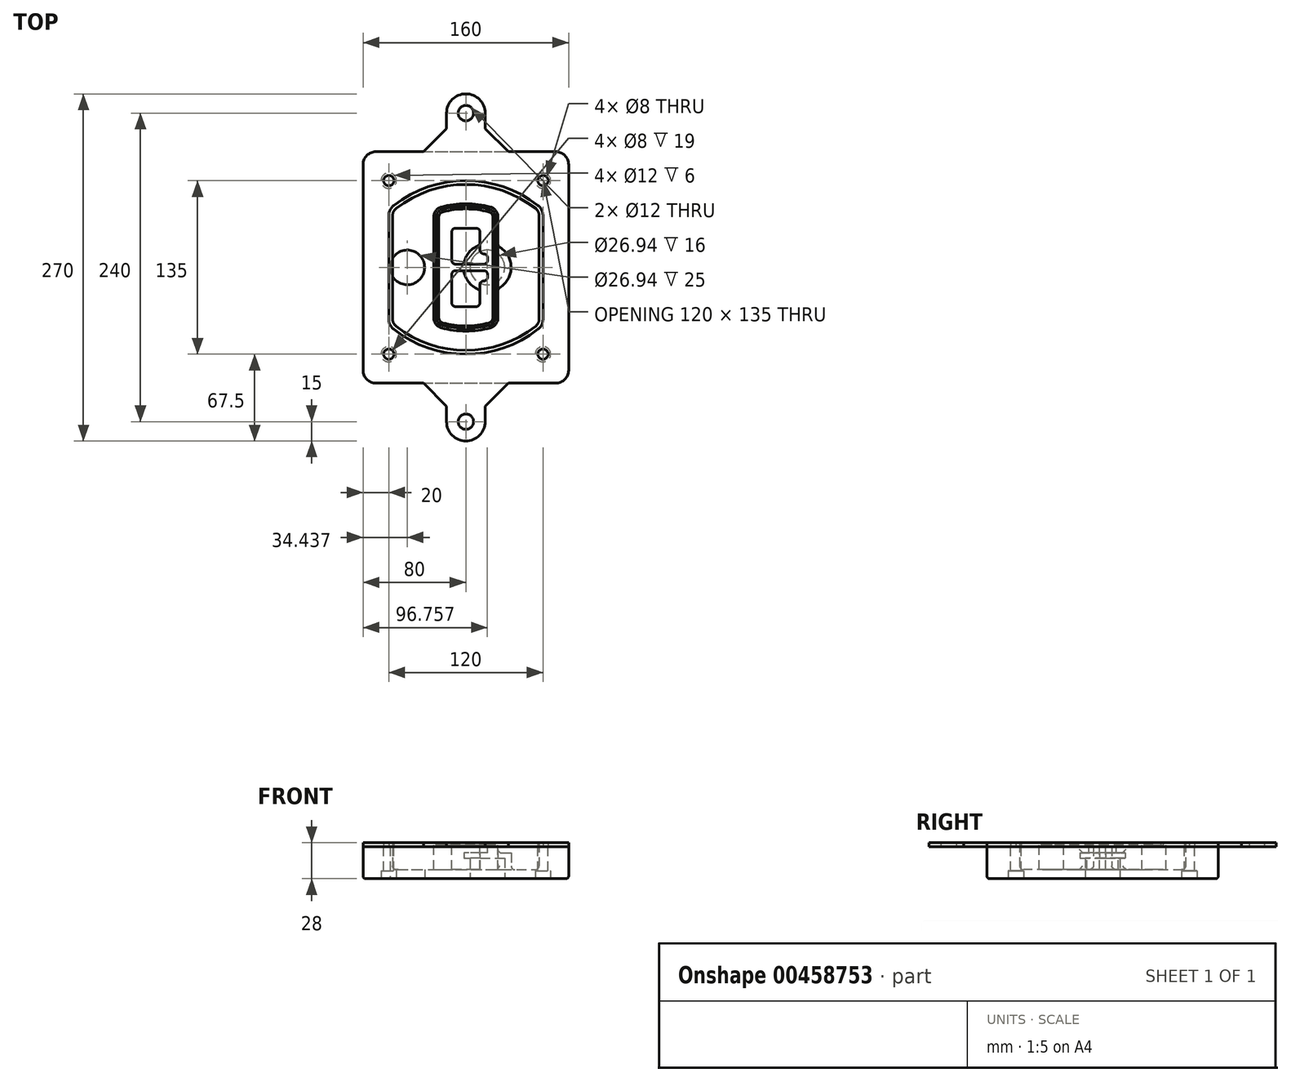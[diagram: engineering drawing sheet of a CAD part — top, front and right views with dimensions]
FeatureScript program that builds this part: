
annotation { "Feature Type Name" : "Feature", "Feature Type Description" : "" }
export const myFeature = defineFeature(function(context is Context, id is Id, definition is map)
    precondition{}
    {
        {
            var Q0;
            Q0=qCreatedBy(makeId("Top.planeOp"),FACE);
            var sketch = newSketch(context, id + "F0", { "sketchPlane" : qUnion([Q0])});
            skPoint(sketch, "E0.rect.middle", {"position": v(0, 0) * mm});
            skLineSegment(sketch, "E1.bottom", {"start": v(-70, -90) * mm, "end": v(70, -90) * mm});
            skLineSegment(sketch, "E1.top", {"start": v(-70, 90) * mm, "end": v(70, 90) * mm});
            skLineSegment(sketch, "E1.left", {"start": v(-80, -80) * mm, "end": v(-80, 80) * mm});
            skLineSegment(sketch, "E1.right", {"start": v(80, -80) * mm, "end": v(80, 80) * mm});
            skLineSegment(sketch, "E2", {"start": v(-80, 90) * mm, "end": v(80, -90) * mm, "construction": true});
            skLineSegment(sketch, "E3", {"start": v(80, 90) * mm, "end": v(-80, -90) * mm, "construction": true});
            skCircle(sketch, "E4", {"center": v(-60, 67.5) * mm, "radius": 4 * mm});
            skCircle(sketch, "E5", {"center": v(60, 67.5) * mm, "radius": 4 * mm});
            skCircle(sketch, "E6", {"center": v(60, -67.5) * mm, "radius": 4 * mm});
            skCircle(sketch, "E7", {"center": v(-60, -67.5) * mm, "radius": 4 * mm});
            skLineSegment(sketch, "E8", {"start": v(-60, 67.5) * mm, "end": v(60, 67.5) * mm, "construction": true});
            skLineSegment(sketch, "E9", {"start": v(60, 67.5) * mm, "end": v(60, -67.5) * mm, "construction": true});
            skLineSegment(sketch, "E10", {"start": v(60, -67.5) * mm, "end": v(-60, -67.5) * mm, "construction": true});
            skLineSegment(sketch, "E11", {"start": v(-60, -67.5) * mm, "end": v(-60, 67.5) * mm, "construction": true});
            skLineSegment(sketch, "E12", {"start": v(-60, 40.3) * mm, "end": v(-60, -40.3) * mm});
            skLineSegment(sketch, "E13", {"start": v(60, 40.3) * mm, "end": v(60, -40.3) * mm});
            skArc(sketch, "E14", {"start": v(56.15, 48.18) * mm, "mid": v(0, 67.5) * mm, "end": v(-56.15, 48.18) * mm});
            skArc(sketch, "E15", {"start": v(-56.15, -48.18) * mm, "mid": v(0, -67.5) * mm, "end": v(56.15, -48.18) * mm});
            skLineSegment(sketch, "E16", {"start": v(-60, 0) * mm, "end": v(60, 0) * mm, "construction": true});
            skPoint(sketch, "E17.visualSharp", {"position": v(-60, -45) * mm});
            skArc(sketch, "E17.filletArc", {"start": v(-60, -40.3) * mm, "mid": v(-58.99, -44.68) * mm, "end": v(-56.15, -48.18) * mm});
            skPoint(sketch, "E18.visualSharp", {"position": v(-60, 45) * mm});
            skArc(sketch, "E18.filletArc", {"start": v(-56.15, 48.18) * mm, "mid": v(-58.99, 44.68) * mm, "end": v(-60, 40.3) * mm});
            skPoint(sketch, "E19.visualSharp", {"position": v(60, 45) * mm});
            skArc(sketch, "E19.filletArc", {"start": v(60, 40.3) * mm, "mid": v(58.99, 44.68) * mm, "end": v(56.15, 48.18) * mm});
            skPoint(sketch, "E20.visualSharp", {"position": v(60, -45) * mm});
            skArc(sketch, "E20.filletArc", {"start": v(56.15, -48.18) * mm, "mid": v(58.99, -44.68) * mm, "end": v(60, -40.3) * mm});
            skPoint(sketch, "E21.visualSharp", {"position": v(-80, 90) * mm});
            skArc(sketch, "E21.filletArc", {"start": v(-70, 90) * mm, "mid": v(-77.07, 87.07) * mm, "end": v(-80, 80) * mm});
            skPoint(sketch, "E22.visualSharp", {"position": v(80, 90) * mm});
            skArc(sketch, "E22.filletArc", {"start": v(80, 80) * mm, "mid": v(77.07, 87.07) * mm, "end": v(70, 90) * mm});
            skPoint(sketch, "E23.visualSharp", {"position": v(80, -90) * mm});
            skArc(sketch, "E23.filletArc", {"start": v(70, -90) * mm, "mid": v(77.07, -87.07) * mm, "end": v(80, -80) * mm});
            skPoint(sketch, "E24.visualSharp", {"position": v(-80, -90) * mm});
            skArc(sketch, "E24.filletArc", {"start": v(-80, -80) * mm, "mid": v(-77.07, -87.07) * mm, "end": v(-70, -90) * mm});
            skArc(sketch, "E25.0", {"start": v(57, 40.3) * mm, "mid": v(56.3, 43.36) * mm, "end": v(54.3, 45.81) * mm});
            skLineSegment(sketch, "E25.1", {"start": v(57, 40.3) * mm, "end": v(57, -40.3) * mm});
            skArc(sketch, "E25.2", {"start": v(54.3, -45.81) * mm, "mid": v(56.3, -43.36) * mm, "end": v(57, -40.3) * mm});
            skArc(sketch, "E25.3", {"start": v(-54.3, -45.81) * mm, "mid": v(0, -64.5) * mm, "end": v(54.3, -45.81) * mm});
            skArc(sketch, "E25.4", {"start": v(-57, -40.3) * mm, "mid": v(-56.3, -43.36) * mm, "end": v(-54.3, -45.81) * mm});
            skArc(sketch, "E25.5", {"start": v(54.3, 45.81) * mm, "mid": v(0, 64.5) * mm, "end": v(-54.3, 45.81) * mm});
            skLineSegment(sketch, "E25.6", {"start": v(-57, 40.3) * mm, "end": v(-57, -40.3) * mm});
            skArc(sketch, "E25.7", {"start": v(-54.3, 45.81) * mm, "mid": v(-56.3, 43.36) * mm, "end": v(-57, 40.3) * mm});
            skArc(sketch, "E26.0", {"start": v(-58.62, 51.33) * mm, "mid": v(-62.58, 46.43) * mm, "end": v(-64, 40.3) * mm});
            skArc(sketch, "E26.1", {"start": v(58.62, 51.33) * mm, "mid": v(0, 71.5) * mm, "end": v(-58.62, 51.33) * mm});
            skArc(sketch, "E26.2", {"start": v(64, 40.3) * mm, "mid": v(62.58, 46.43) * mm, "end": v(58.62, 51.33) * mm});
            skLineSegment(sketch, "E26.3", {"start": v(64, 40.3) * mm, "end": v(64, -40.3) * mm});
            skArc(sketch, "E26.4", {"start": v(58.62, -51.33) * mm, "mid": v(62.58, -46.43) * mm, "end": v(64, -40.3) * mm});
            skLineSegment(sketch, "E26.5", {"start": v(-64, 40.3) * mm, "end": v(-64, -40.3) * mm});
            skArc(sketch, "E26.6", {"start": v(-58.62, -51.33) * mm, "mid": v(0, -71.5) * mm, "end": v(58.62, -51.33) * mm});
            skArc(sketch, "E26.7", {"start": v(-64, -40.3) * mm, "mid": v(-62.58, -46.43) * mm, "end": v(-58.62, -51.33) * mm});
            skSolve(sketch);
        }
        {
            var Q0;
            Q0=makeQuery(id+"F0.imprint","IMPRINT",FACE,{"disambiguationData":[TD([[makeQuery(id+"F0.imprint","IMPRINT",EDGE,{"derivedFrom":sQuery(id+"F0.wireOp",EDGE,"E1.bottom")}),1.0]])]});
            var Q1;
            Q1=makeQuery(id+"F0.imprint","IMPRINT",FACE,{"disambiguationData":[TD([[makeQuery(id+"F0.imprint","IMPRINT",EDGE,{"derivedFrom":sQuery(id+"F0.wireOp",EDGE,"E12")}),1.0]])]});
            var Q2;
            Q2=makeQuery(id+"F0.imprint","IMPRINT",FACE,{"disambiguationData":[TD([[makeQuery(id+"F0.imprint","IMPRINT",EDGE,{"derivedFrom":sQuery(id+"F0.wireOp",EDGE,"E25.0")}),1.0]])]});
            var Q3;
            Q3=makeQuery(id+"F0.imprint","IMPRINT",FACE,{"disambiguationData":[TD([[makeQuery(id+"F0.imprint","IMPRINT",EDGE,{"derivedFrom":sQuery(id+"F0.wireOp",EDGE,"E12")}),-1.0]])]});
            extrude(context, id + "F1", {"entities" : qUnion([Q0, Q1, Q2, Q3]), "oppositeDirection" : true, "depth" : 25 * mm});
        }
        {
            var Q0;
            Q0=makeQuery(id+"F0.imprint","IMPRINT",FACE,{"disambiguationData":[TD([[makeQuery(id+"F0.imprint","IMPRINT",EDGE,{"derivedFrom":sQuery(id+"F0.wireOp",EDGE,"E12")}),1.0]])]});
            extrude(context, id + "F2", {"entities" : qUnion([Q0]), "operationType" : NewBodyOperationType.ADD, "depth" : 3 * mm});
        }
        {
            var Q0;
            Q0=makeQuery(id+"F0.imprint","IMPRINT",FACE,{"disambiguationData":[TD([[makeQuery(id+"F0.imprint","IMPRINT",EDGE,{"derivedFrom":sQuery(id+"F0.wireOp",EDGE,"E25.0")}),1.0]])]});
            extrude(context, id + "F3", {"entities" : qUnion([Q0]), "operationType" : NewBodyOperationType.REMOVE, "oppositeDirection" : true, "depth" : 18 * mm});
        }
        {
            var Q0;
            Q0=makeQuery(id+"F2.opExtrude","CAP_FACE",FACE,{"disambiguationData":[OSD([sQuery(id+"F0.wireOp",EDGE,"E12"),sQuery(id+"F0.wireOp",EDGE,"E13"),sQuery(id+"F0.wireOp",EDGE,"E14"),sQuery(id+"F0.wireOp",EDGE,"E15"),sQuery(id+"F0.wireOp",EDGE,"E17.filletArc"),sQuery(id+"F0.wireOp",EDGE,"E18.filletArc"),sQuery(id+"F0.wireOp",EDGE,"E19.filletArc"),sQuery(id+"F0.wireOp",EDGE,"E20.filletArc"),sQuery(id+"F0.wireOp",EDGE,"E25.0"),sQuery(id+"F0.wireOp",EDGE,"E25.1"),sQuery(id+"F0.wireOp",EDGE,"E25.2"),sQuery(id+"F0.wireOp",EDGE,"E25.3"),sQuery(id+"F0.wireOp",EDGE,"E25.4"),sQuery(id+"F0.wireOp",EDGE,"E25.5"),sQuery(id+"F0.wireOp",EDGE,"E25.6"),sQuery(id+"F0.wireOp",EDGE,"E25.7")])],"isStart":false});
            var sketch = newSketch(context, id + "F4", { "sketchPlane" : qUnion([Q0])});
            skArc(sketch, "E27.0", {"start": v(-19.08, -46.97) * mm, "mid": v(0, -49.5) * mm, "end": v(19.08, -46.97) * mm});
            skArc(sketch, "E28.0", {"start": v(19.08, 46.97) * mm, "mid": v(0, 49.5) * mm, "end": v(-19.08, 46.97) * mm});
            skLineSegment(sketch, "E29", {"start": v(-25, 39.25) * mm, "end": v(-25, -39.25) * mm});
            skLineSegment(sketch, "E30", {"start": v(25, 39.25) * mm, "end": v(25, -39.25) * mm});
            skLineSegment(sketch, "E31", {"start": v(-25, 45.1) * mm, "end": v(25, 45.1) * mm, "construction": true});
            skLineSegment(sketch, "E32", {"start": v(-25, -45.1) * mm, "end": v(25, -45.1) * mm, "construction": true});
            skPoint(sketch, "E33.visualSharp", {"position": v(-25, 45.1) * mm});
            skArc(sketch, "E33.filletArc", {"start": v(-19.08, 46.97) * mm, "mid": v(-23.35, 44.11) * mm, "end": v(-25, 39.25) * mm});
            skPoint(sketch, "E34.visualSharp", {"position": v(25, 45.1) * mm});
            skArc(sketch, "E34.filletArc", {"start": v(25, 39.25) * mm, "mid": v(23.35, 44.11) * mm, "end": v(19.08, 46.97) * mm});
            skPoint(sketch, "E35.visualSharp", {"position": v(25, -45.1) * mm});
            skArc(sketch, "E35.filletArc", {"start": v(19.08, -46.97) * mm, "mid": v(23.35, -44.11) * mm, "end": v(25, -39.25) * mm});
            skPoint(sketch, "E36.visualSharp", {"position": v(-25, -45.1) * mm});
            skArc(sketch, "E36.filletArc", {"start": v(-25, -39.25) * mm, "mid": v(-23.35, -44.11) * mm, "end": v(-19.08, -46.97) * mm});
            skArc(sketch, "E37.0", {"start": v(54.3, 45.81) * mm, "mid": v(0, 64.5) * mm, "end": v(-54.3, 45.81) * mm});
            skArc(sketch, "E37.1", {"start": v(-54.3, 45.81) * mm, "mid": v(-56.3, 43.36) * mm, "end": v(-57, 40.3) * mm});
            skLineSegment(sketch, "E37.2", {"start": v(-57, 40.3) * mm, "end": v(-57, -40.3) * mm});
            skArc(sketch, "E37.3", {"start": v(-57, -40.3) * mm, "mid": v(-56.3, -43.36) * mm, "end": v(-54.3, -45.81) * mm});
            skArc(sketch, "E37.4", {"start": v(-54.3, -45.81) * mm, "mid": v(0, -64.5) * mm, "end": v(54.3, -45.81) * mm});
            skArc(sketch, "E37.5", {"start": v(54.3, -45.81) * mm, "mid": v(56.3, -43.36) * mm, "end": v(57, -40.3) * mm});
            skLineSegment(sketch, "E37.6", {"start": v(57, 40.3) * mm, "end": v(57, -40.3) * mm});
            skArc(sketch, "E37.7", {"start": v(57, 40.3) * mm, "mid": v(56.3, 43.36) * mm, "end": v(54.3, 45.81) * mm});
            skLineSegment(sketch, "E38.0", {"start": v(23, 39.25) * mm, "end": v(23, -39.25) * mm});
            skArc(sketch, "E38.1", {"start": v(18.56, -45.04) * mm, "mid": v(21.76, -42.9) * mm, "end": v(23, -39.25) * mm});
            skArc(sketch, "E38.2", {"start": v(-18.56, -45.04) * mm, "mid": v(0, -47.5) * mm, "end": v(18.56, -45.04) * mm});
            skArc(sketch, "E38.3", {"start": v(-23, -39.25) * mm, "mid": v(-21.76, -42.9) * mm, "end": v(-18.56, -45.04) * mm});
            skLineSegment(sketch, "E38.4", {"start": v(-23, 39.25) * mm, "end": v(-23, -39.25) * mm});
            skArc(sketch, "E38.5", {"start": v(23, 39.25) * mm, "mid": v(21.76, 42.9) * mm, "end": v(18.56, 45.04) * mm});
            skArc(sketch, "E38.6", {"start": v(-18.56, 45.04) * mm, "mid": v(-21.76, 42.9) * mm, "end": v(-23, 39.25) * mm});
            skArc(sketch, "E38.7", {"start": v(18.56, 45.04) * mm, "mid": v(0, 47.5) * mm, "end": v(-18.56, 45.04) * mm});
            skArc(sketch, "E39.0", {"start": v(21, 39.25) * mm, "mid": v(20.18, 41.68) * mm, "end": v(18.04, 43.1) * mm});
            skLineSegment(sketch, "E39.1", {"start": v(21, 39.25) * mm, "end": v(21, -39.25) * mm});
            skArc(sketch, "E39.2", {"start": v(18.04, -43.1) * mm, "mid": v(20.18, -41.68) * mm, "end": v(21, -39.25) * mm});
            skArc(sketch, "E39.3", {"start": v(-18.04, -43.1) * mm, "mid": v(0, -45.5) * mm, "end": v(18.04, -43.1) * mm});
            skArc(sketch, "E39.4", {"start": v(-21, -39.25) * mm, "mid": v(-20.18, -41.68) * mm, "end": v(-18.04, -43.1) * mm});
            skArc(sketch, "E39.5", {"start": v(18.04, 43.1) * mm, "mid": v(0, 45.5) * mm, "end": v(-18.04, 43.1) * mm});
            skLineSegment(sketch, "E39.6", {"start": v(-21, 39.25) * mm, "end": v(-21, -39.25) * mm});
            skArc(sketch, "E39.7", {"start": v(-18.04, 43.1) * mm, "mid": v(-20.18, 41.68) * mm, "end": v(-21, 39.25) * mm});
            skLineSegment(sketch, "E40", {"start": v(-25, 0) * mm, "end": v(25, 0) * mm, "construction": true});
            skLineSegment(sketch, "E41", {"start": v(-11, 5.5) * mm, "end": v(-11, 27.5) * mm});
            skLineSegment(sketch, "E42", {"start": v(-8, 30.5) * mm, "end": v(8, 30.5) * mm});
            skLineSegment(sketch, "E43", {"start": v(11, 27.5) * mm, "end": v(11, 13.5) * mm});
            skLineSegment(sketch, "E44", {"start": v(14, 10.5) * mm, "end": v(14, 10.5) * mm});
            skLineSegment(sketch, "E45", {"start": v(17, 7.5) * mm, "end": v(17, 5.5) * mm});
            skLineSegment(sketch, "E46", {"start": v(14, 2.5) * mm, "end": v(-8, 2.5) * mm});
            skPoint(sketch, "E47.visualSharp", {"position": v(-11, 30.5) * mm});
            skArc(sketch, "E47.filletArc", {"start": v(-8, 30.5) * mm, "mid": v(-10.12, 29.62) * mm, "end": v(-11, 27.5) * mm});
            skPoint(sketch, "E48.visualSharp", {"position": v(11, 30.5) * mm});
            skArc(sketch, "E48.filletArc", {"start": v(11, 27.5) * mm, "mid": v(10.12, 29.62) * mm, "end": v(8, 30.5) * mm});
            skPoint(sketch, "E49.visualSharp", {"position": v(11, 10.5) * mm});
            skArc(sketch, "E49.filletArc", {"start": v(11, 13.5) * mm, "mid": v(11.88, 11.38) * mm, "end": v(14, 10.5) * mm});
            skPoint(sketch, "E50.visualSharp", {"position": v(17, 10.5) * mm});
            skArc(sketch, "E50.filletArc", {"start": v(17, 7.5) * mm, "mid": v(16.12, 9.62) * mm, "end": v(14, 10.5) * mm});
            skPoint(sketch, "E51.visualSharp", {"position": v(17, 2.5) * mm});
            skArc(sketch, "E51.filletArc", {"start": v(14, 2.5) * mm, "mid": v(16.12, 3.38) * mm, "end": v(17, 5.5) * mm});
            skPoint(sketch, "E52.visualSharp", {"position": v(-11, 2.5) * mm});
            skArc(sketch, "E52.filletArc", {"start": v(-11, 5.5) * mm, "mid": v(-10.12, 3.38) * mm, "end": v(-8, 2.5) * mm});
            skLineSegment(sketch, "E53.0.MirrorCS", {"start": v(14, -2.5) * mm, "end": v(-8, -2.5) * mm});
            skArc(sketch, "E54.0.MirrorCS", {"start": v(-11, -5.5) * mm, "mid": v(-10.12, -3.38) * mm, "end": v(-8, -2.5) * mm});
            skLineSegment(sketch, "E55.0.MirrorCS", {"start": v(-11, -5.5) * mm, "end": v(-11, -27.5) * mm});
            skArc(sketch, "E56.0.MirrorCS", {"start": v(-8, -30.5) * mm, "mid": v(-10.12, -29.62) * mm, "end": v(-11, -27.5) * mm});
            skLineSegment(sketch, "E57.0.MirrorCS", {"start": v(-8, -30.5) * mm, "end": v(8, -30.5) * mm});
            skArc(sketch, "E58.0.MirrorCS", {"start": v(11, -27.5) * mm, "mid": v(10.12, -29.62) * mm, "end": v(8, -30.5) * mm});
            skLineSegment(sketch, "E59.0.MirrorCS", {"start": v(11, -27.5) * mm, "end": v(11, -13.5) * mm});
            skArc(sketch, "E60.0.MirrorCS", {"start": v(11, -13.5) * mm, "mid": v(11.88, -11.38) * mm, "end": v(14, -10.5) * mm});
            skArc(sketch, "E61.0.MirrorCS", {"start": v(17, -7.5) * mm, "mid": v(16.12, -9.62) * mm, "end": v(14, -10.5) * mm});
            skLineSegment(sketch, "E62.0.MirrorCS", {"start": v(17, -7.5) * mm, "end": v(17, -5.5) * mm});
            skArc(sketch, "E63.0.MirrorCS", {"start": v(14, -2.5) * mm, "mid": v(16.12, -3.38) * mm, "end": v(17, -5.5) * mm});
            skSolve(sketch);
        }
        {
            var Q0;
            Q0=makeQuery(id+"F4.imprint","IMPRINT",FACE,{"disambiguationData":[TD([[makeQuery(id+"F4.imprint","IMPRINT",EDGE,{"derivedFrom":sQuery(id+"F4.wireOp",EDGE,"E27.0")}),1.0]])]});
            var Q1;
            Q1=makeQuery(id+"F4.imprint","IMPRINT",FACE,{"disambiguationData":[TD([[makeQuery(id+"F4.imprint","IMPRINT",EDGE,{"derivedFrom":sQuery(id+"F4.wireOp",EDGE,"E38.0")}),-1.0]])]});
            var Q2;
            Q2=makeQuery(id+"F4.imprint","IMPRINT",FACE,{"disambiguationData":[TD([[makeQuery(id+"F4.imprint","IMPRINT",EDGE,{"derivedFrom":sQuery(id+"F4.wireOp",EDGE,"E39.0")}),1.0]])]});
            extrude(context, id + "F5", {"entities" : qUnion([Q0, Q1, Q2]), "operationType" : NewBodyOperationType.ADD, "endBound" : BoundingType.UP_TO_NEXT, "oppositeDirection" : true, "depth" : 25 * mm});
        }
        {
            var Q0;
            Q0=makeQuery(id+"F4.imprint","IMPRINT",FACE,{"disambiguationData":[TD([[makeQuery(id+"F4.imprint","IMPRINT",EDGE,{"derivedFrom":sQuery(id+"F4.wireOp",EDGE,"E38.0")}),-1.0]])]});
            extrude(context, id + "F6", {"entities" : qUnion([Q0]), "operationType" : NewBodyOperationType.REMOVE, "oppositeDirection" : true, "depth" : 2 * mm});
        }
        {
            var Q0;
            Q0=makeQuery(id+"F1.opExtrude","CAP_FACE",FACE,{"disambiguationData":[OSD([sQuery(id+"F0.wireOp",EDGE,"E1.bottom"),sQuery(id+"F0.wireOp",EDGE,"E1.top"),sQuery(id+"F0.wireOp",EDGE,"E1.left"),sQuery(id+"F0.wireOp",EDGE,"E1.right"),sQuery(id+"F0.wireOp",EDGE,"E4"),sQuery(id+"F0.wireOp",EDGE,"E5"),sQuery(id+"F0.wireOp",EDGE,"E6"),sQuery(id+"F0.wireOp",EDGE,"E7"),sQuery(id+"F0.wireOp",EDGE,"E21.filletArc"),sQuery(id+"F0.wireOp",EDGE,"E22.filletArc"),sQuery(id+"F0.wireOp",EDGE,"E23.filletArc"),sQuery(id+"F0.wireOp",EDGE,"E24.filletArc")])],"isStart":false});
            var sketch = newSketch(context, id + "F7", { "sketchPlane" : qUnion([Q0])});
            skCircle(sketch, "E64", {"center": v(16.76, 0) * mm, "radius": 13.47 * mm});
            skCircle(sketch, "E65", {"center": v(-45.56, 0) * mm, "radius": 13.47 * mm});
            skLineSegment(sketch, "E66", {"start": v(80, 0) * mm, "end": v(-80, 0) * mm});
            skCircle(sketch, "E67", {"center": v(16.76, 0) * mm, "radius": 18.47 * mm});
            skCircle(sketch, "E68", {"center": v(60, -67.5) * mm, "radius": 6 * mm});
            skCircle(sketch, "E69", {"center": v(-60, -67.5) * mm, "radius": 6 * mm});
            skCircle(sketch, "E70", {"center": v(-60, 67.5) * mm, "radius": 6 * mm});
            skCircle(sketch, "E71", {"center": v(60, 67.5) * mm, "radius": 6 * mm});
            skSolve(sketch);
        }
        {
            var Q0;
            {var subQ1=sQuery(id+"F7.wireOp",EDGE,"E66");var subQ4=sQuery(id+"F7.wireOp",EDGE,"E64");var subQ6=makeQuery(id+"F7.imprint","INTERSECT",VERTEX,{"disambiguationData":[OD(0.0)],"derivedFrom":[subQ4,subQ1]});Q0=makeQuery(id+"F7.imprint","IMPRINT",FACE,{"disambiguationData":[TD([[makeQuery(id+"F7.imprint","IMPRINT",EDGE,{"disambiguationData":[TD([[subQ6,-1.0]])],"derivedFrom":subQ4}),-1.0]])]});}
            var Q1;
            {var subQ0=sQuery(id+"F7.wireOp",EDGE,"E66");var subQ1=sQuery(id+"F7.wireOp",EDGE,"E64");var subQ3=makeQuery(id+"F7.imprint","INTERSECT",VERTEX,{"disambiguationData":[OD(0.0)],"derivedFrom":[subQ1,subQ0]});Q1=makeQuery(id+"F7.imprint","IMPRINT",FACE,{"disambiguationData":[TD([[makeQuery(id+"F7.imprint","IMPRINT",EDGE,{"disambiguationData":[TD([[subQ3,-1.0]])],"derivedFrom":subQ1}),1.0]])]});}
            var Q2;
            {var subQ0=sQuery(id+"F7.wireOp",EDGE,"E66");var subQ1=sQuery(id+"F7.wireOp",EDGE,"E64");var subQ3=makeQuery(id+"F7.imprint","INTERSECT",VERTEX,{"disambiguationData":[OD(0.0)],"derivedFrom":[subQ1,subQ0]});Q2=makeQuery(id+"F7.imprint","IMPRINT",FACE,{"disambiguationData":[TD([[makeQuery(id+"F7.imprint","IMPRINT",EDGE,{"disambiguationData":[TD([[subQ3,1.0]])],"derivedFrom":subQ1}),1.0]])]});}
            var Q3;
            {var subQ1=sQuery(id+"F7.wireOp",EDGE,"E66");var subQ4=sQuery(id+"F7.wireOp",EDGE,"E64");var subQ6=makeQuery(id+"F7.imprint","INTERSECT",VERTEX,{"disambiguationData":[OD(0.0)],"derivedFrom":[subQ4,subQ1]});Q3=makeQuery(id+"F7.imprint","IMPRINT",FACE,{"disambiguationData":[TD([[makeQuery(id+"F7.imprint","IMPRINT",EDGE,{"disambiguationData":[TD([[subQ6,1.0]])],"derivedFrom":subQ4}),-1.0]])]});}
            extrude(context, id + "F8", {"entities" : qUnion([Q0, Q1, Q2, Q3]), "operationType" : NewBodyOperationType.ADD, "oppositeDirection" : true, "depth" : 20 * mm});
        }
        {
            var Q0;
            {var subQ0=sQuery(id+"F7.wireOp",EDGE,"E66");var subQ1=sQuery(id+"F7.wireOp",EDGE,"E64");var subQ3=makeQuery(id+"F7.imprint","INTERSECT",VERTEX,{"disambiguationData":[OD(0.0)],"derivedFrom":[subQ1,subQ0]});Q0=makeQuery(id+"F7.imprint","IMPRINT",FACE,{"disambiguationData":[TD([[makeQuery(id+"F7.imprint","IMPRINT",EDGE,{"disambiguationData":[TD([[subQ3,-1.0]])],"derivedFrom":subQ1}),1.0]])]});}
            var Q1;
            {var subQ0=sQuery(id+"F7.wireOp",EDGE,"E66");var subQ1=sQuery(id+"F7.wireOp",EDGE,"E64");var subQ3=makeQuery(id+"F7.imprint","INTERSECT",VERTEX,{"disambiguationData":[OD(0.0)],"derivedFrom":[subQ1,subQ0]});Q1=makeQuery(id+"F7.imprint","IMPRINT",FACE,{"disambiguationData":[TD([[makeQuery(id+"F7.imprint","IMPRINT",EDGE,{"disambiguationData":[TD([[subQ3,1.0]])],"derivedFrom":subQ1}),1.0]])]});}
            extrude(context, id + "F9", {"entities" : qUnion([Q0, Q1]), "operationType" : NewBodyOperationType.REMOVE, "oppositeDirection" : true, "depth" : 16 * mm});
        }
        {
            var Q0;
            {var subQ0=sQuery(id+"F7.wireOp",EDGE,"E66");var subQ1=sQuery(id+"F7.wireOp",EDGE,"E65");var subQ3=makeQuery(id+"F7.imprint","INTERSECT",VERTEX,{"disambiguationData":[OD(0.0)],"derivedFrom":[subQ1,subQ0]});Q0=makeQuery(id+"F7.imprint","IMPRINT",FACE,{"disambiguationData":[TD([[makeQuery(id+"F7.imprint","IMPRINT",EDGE,{"disambiguationData":[TD([[subQ3,-1.0]])],"derivedFrom":subQ1}),1.0]])]});}
            var Q1;
            {var subQ0=sQuery(id+"F7.wireOp",EDGE,"E66");var subQ1=sQuery(id+"F7.wireOp",EDGE,"E65");var subQ3=makeQuery(id+"F7.imprint","INTERSECT",VERTEX,{"disambiguationData":[OD(0.0)],"derivedFrom":[subQ1,subQ0]});Q1=makeQuery(id+"F7.imprint","IMPRINT",FACE,{"disambiguationData":[TD([[makeQuery(id+"F7.imprint","IMPRINT",EDGE,{"disambiguationData":[TD([[subQ3,1.0]])],"derivedFrom":subQ1}),1.0]])]});}
            extrude(context, id + "F10", {"entities" : qUnion([Q0, Q1]), "operationType" : NewBodyOperationType.REMOVE, "oppositeDirection" : true, "depth" : 25 * mm});
        }
        {
            var Q0;
            Q0=makeQuery(id+"F7.imprint","IMPRINT",FACE,{"disambiguationData":[TD([[makeQuery(id+"F7.imprint","IMPRINT",EDGE,{"derivedFrom":sQuery(id+"F7.wireOp",EDGE,"E68")}),1.0]])]});
            var Q1;
            Q1=makeQuery(id+"F7.imprint","IMPRINT",FACE,{"disambiguationData":[TD([[makeQuery(id+"F7.imprint","IMPRINT",EDGE,{"derivedFrom":makeQuery(id+"F1.opExtrude","CAP_EDGE",EDGE,{"disambiguationData":[OSD([sQuery(id+"F0.wireOp",EDGE,"E5")])],"isStart":false})}),-1.0]])]});
            var Q2;
            Q2=makeQuery(id+"F7.imprint","IMPRINT",FACE,{"disambiguationData":[TD([[makeQuery(id+"F7.imprint","IMPRINT",EDGE,{"derivedFrom":sQuery(id+"F7.wireOp",EDGE,"E69")}),1.0]])]});
            var Q3;
            Q3=makeQuery(id+"F7.imprint","IMPRINT",FACE,{"disambiguationData":[TD([[makeQuery(id+"F7.imprint","IMPRINT",EDGE,{"derivedFrom":makeQuery(id+"F1.opExtrude","CAP_EDGE",EDGE,{"disambiguationData":[OSD([sQuery(id+"F0.wireOp",EDGE,"E4")])],"isStart":false})}),-1.0]])]});
            var Q4;
            Q4=makeQuery(id+"F7.imprint","IMPRINT",FACE,{"disambiguationData":[TD([[makeQuery(id+"F7.imprint","IMPRINT",EDGE,{"derivedFrom":sQuery(id+"F7.wireOp",EDGE,"E70")}),1.0]])]});
            var Q5;
            Q5=makeQuery(id+"F7.imprint","IMPRINT",FACE,{"disambiguationData":[TD([[makeQuery(id+"F7.imprint","IMPRINT",EDGE,{"derivedFrom":makeQuery(id+"F1.opExtrude","CAP_EDGE",EDGE,{"disambiguationData":[OSD([sQuery(id+"F0.wireOp",EDGE,"E7")])],"isStart":false})}),-1.0]])]});
            var Q6;
            Q6=makeQuery(id+"F7.imprint","IMPRINT",FACE,{"disambiguationData":[TD([[makeQuery(id+"F7.imprint","IMPRINT",EDGE,{"derivedFrom":sQuery(id+"F7.wireOp",EDGE,"E71")}),1.0]])]});
            var Q7;
            Q7=makeQuery(id+"F7.imprint","IMPRINT",FACE,{"disambiguationData":[TD([[makeQuery(id+"F7.imprint","IMPRINT",EDGE,{"derivedFrom":makeQuery(id+"F1.opExtrude","CAP_EDGE",EDGE,{"disambiguationData":[OSD([sQuery(id+"F0.wireOp",EDGE,"E6")])],"isStart":false})}),-1.0]])]});
            extrude(context, id + "F11", {"entities" : qUnion([Q0, Q1, Q2, Q3, Q4, Q5, Q6, Q7]), "operationType" : NewBodyOperationType.REMOVE, "oppositeDirection" : true, "depth" : 6 * mm});
        }
        {
            var Q0;
            Q0=makeQuery(id+"F9.boolean.opBoolean","COPY",FACE,{"derivedFrom":makeQuery(id+"F9.opExtrude","CAP_FACE",FACE,{"disambiguationData":[OSD([sQuery(id+"F7.wireOp",EDGE,"E64")])],"isStart":false})});
            var sketch = newSketch(context, id + "F12", { "sketchPlane" : qUnion([Q0])});
            skArc(sketch, "E72.0", {"start": v(11, 17.55) * mm, "mid": v(2.57, 11.82) * mm, "end": v(-1.54, 2.5) * mm});
            skArc(sketch, "E72.1", {"start": v(-1.54, -2.5) * mm, "mid": v(2.57, -11.82) * mm, "end": v(11, -17.55) * mm});
            skLineSegment(sketch, "E73", {"start": v(-1.54, -2.5) * mm, "end": v(14, -2.5) * mm});
            skLineSegment(sketch, "E74.0", {"start": v(14, 2.5) * mm, "end": v(-1.54, 2.5) * mm});
            skArc(sketch, "E74.1", {"start": v(14, 2.5) * mm, "mid": v(16.12, 3.38) * mm, "end": v(17, 5.5) * mm});
            skLineSegment(sketch, "E74.2", {"start": v(17, 7.5) * mm, "end": v(17, 5.5) * mm});
            skArc(sketch, "E74.3", {"start": v(17, 7.5) * mm, "mid": v(16.12, 9.62) * mm, "end": v(14, 10.5) * mm});
            skArc(sketch, "E74.4", {"start": v(11, 13.5) * mm, "mid": v(11.88, 11.38) * mm, "end": v(14, 10.5) * mm});
            skLineSegment(sketch, "E74.5", {"start": v(11, 17.55) * mm, "end": v(11, 13.5) * mm});
            skLineSegment(sketch, "E74.7", {"start": v(14, -2.5) * mm, "end": v(-1.54, -2.5) * mm});
            skArc(sketch, "E74.8", {"start": v(14, -2.5) * mm, "mid": v(16.12, -3.38) * mm, "end": v(17, -5.5) * mm});
            skLineSegment(sketch, "E74.9", {"start": v(17, -7.5) * mm, "end": v(17, -5.5) * mm});
            skArc(sketch, "E74.10", {"start": v(17, -7.5) * mm, "mid": v(16.12, -9.62) * mm, "end": v(14, -10.5) * mm});
            skArc(sketch, "E74.11", {"start": v(11, -13.5) * mm, "mid": v(11.88, -11.38) * mm, "end": v(14, -10.5) * mm});
            skLineSegment(sketch, "E74.12", {"start": v(11, -17.55) * mm, "end": v(11, -13.5) * mm});
            skPoint(sketch, "E75.orphan", {"position": v(11, -27.5) * mm});
            skPoint(sketch, "E76.orphan", {"position": v(-8, -2.5) * mm});
            skPoint(sketch, "E77.orphan", {"position": v(-8, 2.5) * mm});
            skPoint(sketch, "E78.orphan", {"position": v(11, 27.5) * mm});
            skSolve(sketch);
        }
        {
            var Q0;
            {var subQ7=sQuery(id+"F12.wireOp",EDGE,"E72.0");var subQ14=sQuery(id+"F12.wireOp",EDGE,"E72.1");var subQ16=sQuery(id+"F12.wireOp",EDGE,"E74.1");var subQ18=sQuery(id+"F12.wireOp",EDGE,"E74.8");Q0=qUnion([makeQuery(id+"F12.imprint","IMPRINT",FACE,{"disambiguationData":[TD([[makeQuery(id+"F12.imprint","IMPRINT",EDGE,{"derivedFrom":subQ7}),1.0]])]}),makeQuery(id+"F12.imprint","IMPRINT",FACE,{"disambiguationData":[TD([[makeQuery(id+"F12.imprint","IMPRINT",EDGE,{"derivedFrom":subQ14}),1.0]])]}),makeQuery(id+"F12.imprint","IMPRINT",FACE,{"disambiguationData":[TD([[makeQuery(id+"F12.imprint","IMPRINT",EDGE,{"derivedFrom":subQ16}),1.0]])]}),makeQuery(id+"F12.imprint","IMPRINT",FACE,{"disambiguationData":[TD([[makeQuery(id+"F12.imprint","IMPRINT",EDGE,{"derivedFrom":subQ18}),-1.0]])]})]);}
            var Q1;
            Q1=makeQuery(id+"F5.boolean.opBoolean","SPLIT",FACE,{"disambiguationData":[TD([makeQuery(id+"F5.opExtrude","SWEPT_FACE",FACE,{"disambiguationData":[OSD([sQuery(id+"F4.wireOp",EDGE,"E41")])]})])],"derivedFrom":makeQuery(id+"F3.boolean.opBoolean","COPY",FACE,{"derivedFrom":makeQuery(id+"F3.opExtrude","CAP_FACE",FACE,{"disambiguationData":[OSD([sQuery(id+"F0.wireOp",EDGE,"E25.0"),sQuery(id+"F0.wireOp",EDGE,"E25.1"),sQuery(id+"F0.wireOp",EDGE,"E25.2"),sQuery(id+"F0.wireOp",EDGE,"E25.3"),sQuery(id+"F0.wireOp",EDGE,"E25.4"),sQuery(id+"F0.wireOp",EDGE,"E25.5"),sQuery(id+"F0.wireOp",EDGE,"E25.6"),sQuery(id+"F0.wireOp",EDGE,"E25.7")])],"isStart":false})})});
            extrude(context, id + "F13", {"entities" : qUnion([Q0]), "operationType" : NewBodyOperationType.REMOVE, "endBound" : BoundingType.UP_TO_SURFACE, "endBoundEntityFace" : qUnion([Q1]), "depth" : 25 * mm});
        }
        {
            var Q0;
            Q0=makeQuery(id+"F3.boolean.opBoolean","COPY",EDGE,{"derivedFrom":makeQuery(id+"F3.opExtrude","CAP_EDGE",EDGE,{"disambiguationData":[OSD([sQuery(id+"F0.wireOp",EDGE,"E25.6")])],"isStart":false})});
            var Q1;
            Q1=makeQuery(id+"F8.boolean.opBoolean","INTERSECT",EDGE,{"derivedFrom":[makeQuery(id+"F5.opExtrude","SWEPT_FACE",FACE,{"disambiguationData":[OSD([sQuery(id+"F4.wireOp",EDGE,"E30")])]}),makeQuery(id+"F8.opExtrude","CAP_FACE",FACE,{"disambiguationData":[OSD([sQuery(id+"F7.wireOp",EDGE,"E67")])],"isStart":false})]});
            var Q2;
            Q2=makeQuery(id+"F8.boolean.opBoolean","INTERSECT",EDGE,{"disambiguationData":[OD(1.0)],"derivedFrom":[makeQuery(id+"F5.opExtrude","SWEPT_FACE",FACE,{"disambiguationData":[OSD([sQuery(id+"F4.wireOp",EDGE,"E30")])]}),makeQuery(id+"F8.opExtrude","SWEPT_FACE",FACE,{"disambiguationData":[OSD([sQuery(id+"F7.wireOp",EDGE,"E67")])]})]});
            var Q3;
            {var subQ0=sQuery(id+"F4.wireOp",EDGE,"E30");Q3=makeQuery(id+"F8.boolean.opBoolean","SPLIT",EDGE,{"disambiguationData":[TD([makeQuery(id+"F5.opExtrude","SWEPT_FACE",FACE,{"disambiguationData":[OSD([sQuery(id+"F4.wireOp",EDGE,"E35.filletArc")])]})])],"derivedFrom":makeQuery(id+"F5.opExtrude","CAP_EDGE",EDGE,{"disambiguationData":[OSD([subQ0])],"isStart":false})});}
            var Q4;
            {var subQ0=sQuery(id+"F0.wireOp",EDGE,"E25.7");var subQ1=sQuery(id+"F0.wireOp",EDGE,"E25.1");var subQ2=sQuery(id+"F0.wireOp",EDGE,"E25.6");var subQ3=sQuery(id+"F0.wireOp",EDGE,"E25.5");var subQ4=sQuery(id+"F0.wireOp",EDGE,"E25.4");var subQ5=sQuery(id+"F0.wireOp",EDGE,"E25.0");var subQ6=sQuery(id+"F0.wireOp",EDGE,"E25.2");var subQ7=sQuery(id+"F0.wireOp",EDGE,"E25.3");Q4=makeQuery(id+"F8.boolean.opBoolean","INTERSECT",EDGE,{"derivedFrom":[makeQuery(id+"F5.boolean.opBoolean","SPLIT",FACE,{"disambiguationData":[TD([makeQuery(id+"F2.opExtrude","SWEPT_FACE",FACE,{"disambiguationData":[OSD([subQ5])]})])],"derivedFrom":makeQuery(id+"F3.boolean.opBoolean","COPY",FACE,{"derivedFrom":makeQuery(id+"F3.opExtrude","CAP_FACE",FACE,{"disambiguationData":[OSD([subQ5,subQ1,subQ6,subQ7,subQ4,subQ3,subQ2,subQ0])],"isStart":false})})}),makeQuery(id+"F8.opExtrude","SWEPT_FACE",FACE,{"disambiguationData":[OSD([sQuery(id+"F7.wireOp",EDGE,"E67")])]})]});}
            var Q5;
            Q5=makeQuery(id+"F8.boolean.opBoolean","INTERSECT",EDGE,{"disambiguationData":[OD(0.0)],"derivedFrom":[makeQuery(id+"F5.opExtrude","SWEPT_FACE",FACE,{"disambiguationData":[OSD([sQuery(id+"F4.wireOp",EDGE,"E30")])]}),makeQuery(id+"F8.opExtrude","SWEPT_FACE",FACE,{"disambiguationData":[OSD([sQuery(id+"F7.wireOp",EDGE,"E67")])]})]});
            fillet(context, id + "F14", {"entities" : qUnion([Q0, Q1, Q2, Q3, Q4, Q5]), "radius" : 3 * mm, "tangentPropagation" : true, "allowEdgeOverflow" : false});
        }
        {
            var Q0;
            Q0=makeQuery(id+"F1.opExtrude","CAP_EDGE",EDGE,{"disambiguationData":[OSD([sQuery(id+"F0.wireOp",EDGE,"E1.bottom")])],"isStart":false});
            fillet(context, id + "F15", {"entities" : qUnion([Q0]), "radius" : 2 * mm, "tangentPropagation" : true, "allowEdgeOverflow" : false});
        }
        {
            var Q0;
            {var subQ0=sQuery(id+"F0.wireOp",EDGE,"E21.filletArc");var subQ1=sQuery(id+"F0.wireOp",EDGE,"E7");var subQ2=sQuery(id+"F0.wireOp",EDGE,"E6");var subQ3=sQuery(id+"F0.wireOp",EDGE,"E5");var subQ4=sQuery(id+"F0.wireOp",EDGE,"E4");var subQ5=sQuery(id+"F0.wireOp",EDGE,"E22.filletArc");var subQ6=sQuery(id+"F0.wireOp",EDGE,"E1.bottom");var subQ7=sQuery(id+"F0.wireOp",EDGE,"E1.right");var subQ8=sQuery(id+"F0.wireOp",EDGE,"E1.top");var subQ9=sQuery(id+"F0.wireOp",EDGE,"E1.left");var subQ10=sQuery(id+"F0.wireOp",EDGE,"E23.filletArc");var subQ11=sQuery(id+"F0.wireOp",EDGE,"E24.filletArc");Q0=makeQuery(id+"F2.boolean.opBoolean","SPLIT",FACE,{"disambiguationData":[TD([makeQuery(id+"F1.opExtrude","SWEPT_FACE",FACE,{"disambiguationData":[OSD([subQ6])]})])],"derivedFrom":makeQuery(id+"F1.opExtrude","CAP_FACE",FACE,{"disambiguationData":[OSD([subQ6,subQ8,subQ9,subQ7,subQ4,subQ3,subQ2,subQ1,subQ0,subQ5,subQ10,subQ11])],"isStart":true})});}
            var sketch = newSketch(context, id + "F16", { "sketchPlane" : qUnion([Q0])});
            skLineSegment(sketch, "E79", {"start": v(0, 90) * mm, "end": v(0, 120) * mm, "construction": true});
            skLineSegment(sketch, "E80.0", {"start": v(-70, 90) * mm, "end": v(70, 90) * mm});
            skArc(sketch, "E80.1", {"start": v(-70, 90) * mm, "mid": v(-77.07, 87.07) * mm, "end": v(-80, 80) * mm});
            skLineSegment(sketch, "E80.2", {"start": v(-80, -80) * mm, "end": v(-80, 80) * mm});
            skArc(sketch, "E80.3", {"start": v(-80, -80) * mm, "mid": v(-77.07, -87.07) * mm, "end": v(-70, -90) * mm});
            skLineSegment(sketch, "E80.4", {"start": v(-70, -90) * mm, "end": v(70, -90) * mm});
            skArc(sketch, "E80.5", {"start": v(70, -90) * mm, "mid": v(77.07, -87.07) * mm, "end": v(80, -80) * mm});
            skLineSegment(sketch, "E80.6", {"start": v(80, -80) * mm, "end": v(80, 80) * mm});
            skArc(sketch, "E80.7", {"start": v(80, 80) * mm, "mid": v(77.07, 87.07) * mm, "end": v(70, 90) * mm});
            skLineSegment(sketch, "E81.0", {"start": v(-60, 40.3) * mm, "end": v(-60, -40.3) * mm});
            skArc(sketch, "E81.1", {"start": v(-56.15, 48.18) * mm, "mid": v(-58.99, 44.68) * mm, "end": v(-60, 40.3) * mm});
            skArc(sketch, "E81.2", {"start": v(56.15, 48.18) * mm, "mid": v(0, 67.5) * mm, "end": v(-56.15, 48.18) * mm});
            skArc(sketch, "E81.3", {"start": v(60, 40.3) * mm, "mid": v(58.99, 44.68) * mm, "end": v(56.15, 48.18) * mm});
            skLineSegment(sketch, "E81.4", {"start": v(60, 40.3) * mm, "end": v(60, -40.3) * mm});
            skArc(sketch, "E81.5", {"start": v(-56.15, -48.18) * mm, "mid": v(0, -67.5) * mm, "end": v(56.15, -48.18) * mm});
            skArc(sketch, "E81.6", {"start": v(56.15, -48.18) * mm, "mid": v(58.99, -44.68) * mm, "end": v(60, -40.3) * mm});
            skArc(sketch, "E81.7", {"start": v(-60, -40.3) * mm, "mid": v(-58.99, -44.68) * mm, "end": v(-56.15, -48.18) * mm});
            skCircle(sketch, "E81.8", {"center": v(-60, -67.5) * mm, "radius": 4 * mm});
            skCircle(sketch, "E81.9", {"center": v(-60, 67.5) * mm, "radius": 4 * mm});
            skCircle(sketch, "E81.10", {"center": v(60, 67.5) * mm, "radius": 4 * mm});
            skCircle(sketch, "E81.11", {"center": v(60, -67.5) * mm, "radius": 4 * mm});
            skCircle(sketch, "E82", {"center": v(0, 120) * mm, "radius": 6 * mm});
            skLineSegment(sketch, "E83", {"start": v(-15, 108) * mm, "end": v(-33, 90) * mm});
            skLineSegment(sketch, "E84", {"start": v(15, 108) * mm, "end": v(33, 90) * mm});
            skArc(sketch, "E85", {"start": v(-15, 120) * mm, "mid": v(0, 135) * mm, "end": v(15, 120) * mm});
            skLineSegment(sketch, "E86", {"start": v(-15, 120) * mm, "end": v(-15, 108) * mm});
            skLineSegment(sketch, "E87", {"start": v(15, 120) * mm, "end": v(15, 108) * mm});
            skLineSegment(sketch, "E88", {"start": v(-98.05, 0) * mm, "end": v(96.76, 0) * mm, "construction": true});
            skPoint(sketch, "E88.startSnap0", {"position": v(-80, 0) * mm});
            skPoint(sketch, "E88.endSnap0", {"position": v(80, 0) * mm});
            skLineSegment(sketch, "E89.MirrorCS", {"start": v(-15, -108) * mm, "end": v(-33, -90) * mm});
            skLineSegment(sketch, "E90.MirrorCS", {"start": v(-15, -120) * mm, "end": v(-15, -108) * mm});
            skArc(sketch, "E91.MirrorCS", {"start": v(-15, -120) * mm, "mid": v(0, -135) * mm, "end": v(15, -120) * mm});
            skCircle(sketch, "E92.MirrorC", {"center": v(0, -120) * mm, "radius": 6 * mm});
            skLineSegment(sketch, "E93.MirrorCS", {"start": v(0, -90) * mm, "end": v(0, -120) * mm, "construction": true});
            skLineSegment(sketch, "E94.MirrorCS", {"start": v(15, -120) * mm, "end": v(15, -108) * mm});
            skLineSegment(sketch, "E95.MirrorCS", {"start": v(15, -108) * mm, "end": v(33, -90) * mm});
            skSolve(sketch);
        }
        {
            var Q0;
            Q0 = qSketchRegion(id + "F16", true);
            var Q1;
            Q1=makeQuery(id+"F2.opExtrude","CAP_FACE",FACE,{"disambiguationData":[OSD([sQuery(id+"F0.wireOp",EDGE,"E12"),sQuery(id+"F0.wireOp",EDGE,"E13"),sQuery(id+"F0.wireOp",EDGE,"E14"),sQuery(id+"F0.wireOp",EDGE,"E15"),sQuery(id+"F0.wireOp",EDGE,"E17.filletArc"),sQuery(id+"F0.wireOp",EDGE,"E18.filletArc"),sQuery(id+"F0.wireOp",EDGE,"E19.filletArc"),sQuery(id+"F0.wireOp",EDGE,"E20.filletArc"),sQuery(id+"F0.wireOp",EDGE,"E25.0"),sQuery(id+"F0.wireOp",EDGE,"E25.1"),sQuery(id+"F0.wireOp",EDGE,"E25.2"),sQuery(id+"F0.wireOp",EDGE,"E25.3"),sQuery(id+"F0.wireOp",EDGE,"E25.4"),sQuery(id+"F0.wireOp",EDGE,"E25.5"),sQuery(id+"F0.wireOp",EDGE,"E25.6"),sQuery(id+"F0.wireOp",EDGE,"E25.7")])],"isStart":false});
            extrude(context, id + "F17", {"entities" : qUnion([Q0]), "endBound" : BoundingType.UP_TO_SURFACE, "endBoundEntityFace" : qUnion([Q1]), "depth" : 25 * mm});
        }
    });
